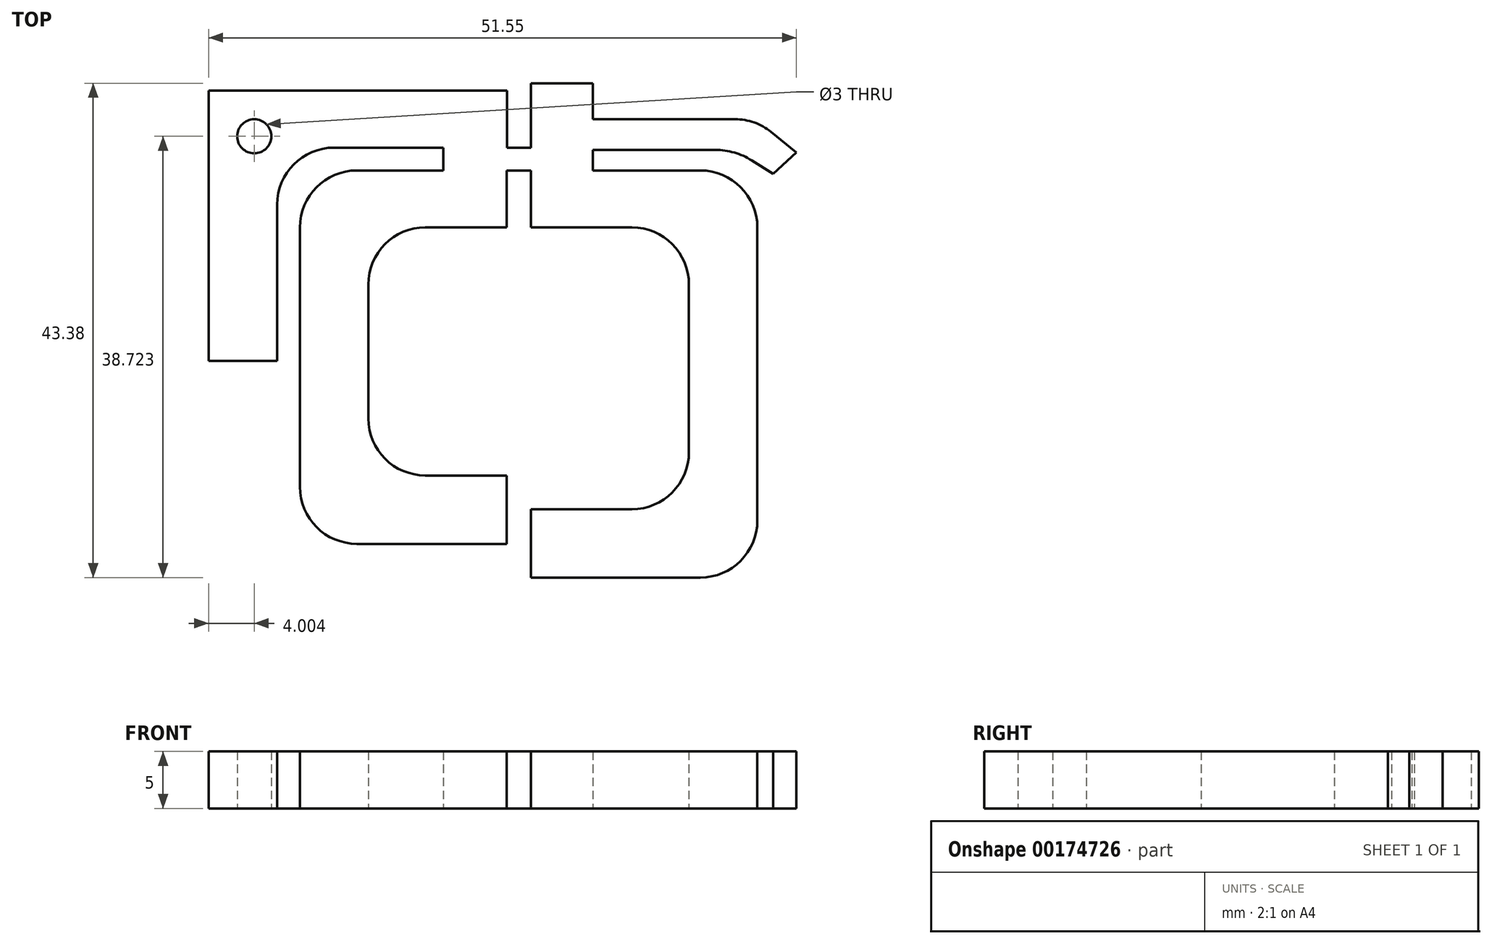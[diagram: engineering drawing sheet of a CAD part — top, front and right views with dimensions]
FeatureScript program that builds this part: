
annotation { "Feature Type Name" : "Feature", "Feature Type Description" : "" }
export const myFeature = defineFeature(function(context is Context, id is Id, definition is map)
    precondition{}
    {
        {
            var Q0;
            Q0=qCreatedBy(makeId("Top.planeOp"),FACE);
            var sketch = newSketch(context, id + "F0", { "sketchPlane" : qUnion([Q0])});
            skLineSegment(sketch, "E0.bottom", {"start": v(-10.9, 25.3) * mm, "end": v(-20.47, 25.3) * mm});
            skLineSegment(sketch, "E0.top", {"start": v(-5.3, 30.3) * mm, "end": v(-31.47, 30.3) * mm});
            skLineSegment(sketch, "E0.left", {"start": v(-5.3, 25.3) * mm, "end": v(-5.3, 30.3) * mm});
            skLineSegment(sketch, "E0.right", {"start": v(-31.47, 26.54) * mm, "end": v(-31.47, 30.3) * mm});
            skLineSegment(sketch, "E1.top", {"start": v(-31.47, 6.6) * mm, "end": v(-25.47, 6.6) * mm});
            skLineSegment(sketch, "E1.left", {"start": v(-31.47, 26.54) * mm, "end": v(-31.47, 6.6) * mm});
            skLineSegment(sketch, "E1.right", {"start": v(-25.47, 20.3) * mm, "end": v(-25.47, 6.6) * mm});
            skArc(sketch, "E2.filletArc", {"start": v(-20.47, 25.3) * mm, "mid": v(-24, 23.84) * mm, "end": v(-25.47, 20.3) * mm});
            skLineSegment(sketch, "E3.right", {"start": v(-10.9, 25.3) * mm, "end": v(-10.9, 23.3) * mm});
            skLineSegment(sketch, "E4.bottom", {"start": v(-10.9, 23.3) * mm, "end": v(-18.47, 23.3) * mm});
            skLineSegment(sketch, "E4.top", {"start": v(-5.33, 18.3) * mm, "end": v(-12.47, 18.3) * mm});
            skLineSegment(sketch, "E4.left", {"start": v(-5.33, 23.3) * mm, "end": v(-5.33, 18.3) * mm});
            skLineSegment(sketch, "E4.right", {"start": v(-23.47, 18.3) * mm, "end": v(-23.47, 9.2) * mm});
            skLineSegment(sketch, "E5.left", {"start": v(-23.47, 15.1) * mm, "end": v(-23.47, -4.46) * mm});
            skLineSegment(sketch, "E5.right", {"start": v(-17.47, 13.3) * mm, "end": v(-17.47, 1.54) * mm});
            skLineSegment(sketch, "E6.top", {"start": v(-12.47, -3.46) * mm, "end": v(-5.33, -3.46) * mm});
            skLineSegment(sketch, "E6.right", {"start": v(-5.33, -9.46) * mm, "end": v(-5.33, -3.46) * mm});
            skPoint(sketch, "E7.visualSharp", {"position": v(-23.47, 23.3) * mm});
            skArc(sketch, "E7.filletArc", {"start": v(-18.47, 23.3) * mm, "mid": v(-22, 21.84) * mm, "end": v(-23.47, 18.3) * mm});
            skArc(sketch, "E8.filletArc", {"start": v(-12.47, 18.3) * mm, "mid": v(-16, 16.84) * mm, "end": v(-17.47, 13.3) * mm});
            skPoint(sketch, "E9.visualSharp", {"position": v(-23.47, -9.46) * mm});
            skArc(sketch, "E9.filletArc", {"start": v(-23.47, -4.46) * mm, "mid": v(-22, -8) * mm, "end": v(-18.47, -9.46) * mm});
            skArc(sketch, "E10.filletArc", {"start": v(-17.47, 1.54) * mm, "mid": v(-16, -2) * mm, "end": v(-12.47, -3.46) * mm});
            skLineSegment(sketch, "E11.bottom", {"start": v(-5.3, 25.3) * mm, "end": v(-3.2, 25.3) * mm});
            skLineSegment(sketch, "E11.top", {"start": v(-5.33, 23.3) * mm, "end": v(-3.2, 23.3) * mm});
            skLineSegment(sketch, "E12.bottom", {"start": v(-3.2, 18.3) * mm, "end": v(2.2, 18.3) * mm});
            skLineSegment(sketch, "E12.top", {"start": v(-3.2, 30.96) * mm, "end": v(2.2, 30.96) * mm});
            skLineSegment(sketch, "E12.left", {"start": v(-3.2, 18.3) * mm, "end": v(-3.2, 23.3) * mm});
            skLineSegment(sketch, "E12.right", {"start": v(2.2, 23.3) * mm, "end": v(2.2, 25.1) * mm});
            skLineSegment(sketch, "E13.bottom", {"start": v(2.2, 23.3) * mm, "end": v(11.65, 23.3) * mm});
            skLineSegment(sketch, "E13.top", {"start": v(2.2, 18.3) * mm, "end": v(5.65, 18.3) * mm});
            skLineSegment(sketch, "E13.right", {"start": v(16.65, 18.3) * mm, "end": v(16.65, 18.3) * mm});
            skLineSegment(sketch, "E14.top", {"start": v(11.65, -12.42) * mm, "end": v(10.65, -12.42) * mm});
            skLineSegment(sketch, "E14.left", {"start": v(16.65, 18.3) * mm, "end": v(16.65, -7.42) * mm});
            skLineSegment(sketch, "E14.right", {"start": v(10.65, 13.3) * mm, "end": v(10.65, -1.42) * mm});
            skLineSegment(sketch, "E15.bottom", {"start": v(10.65, -12.42) * mm, "end": v(-3.2, -12.42) * mm});
            skLineSegment(sketch, "E15.top", {"start": v(5.65, -6.42) * mm, "end": v(-3.2, -6.42) * mm});
            skLineSegment(sketch, "E15.right", {"start": v(-3.2, -12.42) * mm, "end": v(-3.2, -6.42) * mm});
            skLineSegment(sketch, "E16.trimOffspring", {"start": v(-3.2, 25.3) * mm, "end": v(-3.2, 30.96) * mm});
            skPoint(sketch, "E17.visualSharp", {"position": v(16.65, 23.3) * mm});
            skArc(sketch, "E17.filletArc", {"start": v(16.65, 18.3) * mm, "mid": v(15.19, 21.84) * mm, "end": v(11.65, 23.3) * mm});
            skPoint(sketch, "E18.visualSharp", {"position": v(10.65, 18.3) * mm});
            skArc(sketch, "E18.filletArc", {"start": v(10.65, 13.3) * mm, "mid": v(9.19, 16.84) * mm, "end": v(5.65, 18.3) * mm});
            skPoint(sketch, "E19.visualSharp", {"position": v(16.65, -12.42) * mm});
            skArc(sketch, "E19.filletArc", {"start": v(11.65, -12.42) * mm, "mid": v(15.19, -10.95) * mm, "end": v(16.65, -7.42) * mm});
            skPoint(sketch, "E20.visualSharp", {"position": v(10.65, -6.42) * mm});
            skArc(sketch, "E20.filletArc", {"start": v(5.65, -6.42) * mm, "mid": v(9.19, -4.95) * mm, "end": v(10.65, -1.42) * mm});
            skLineSegment(sketch, "E21.trimOffspring", {"start": v(-18.47, -9.46) * mm, "end": v(-5.33, -9.46) * mm});
            skLineSegment(sketch, "E22", {"start": v(2.2, 27.8) * mm, "end": v(14.7, 27.8) * mm});
            skLineSegment(sketch, "E23", {"start": v(17.85, 26.68) * mm, "end": v(20.08, 24.87) * mm});
            skPoint(sketch, "E24.visualSharp", {"position": v(16.47, 27.8) * mm});
            skArc(sketch, "E24.filletArc", {"start": v(17.85, 26.68) * mm, "mid": v(16.37, 27.51) * mm, "end": v(14.7, 27.8) * mm});
            skLineSegment(sketch, "E25", {"start": v(2.2, 25.1) * mm, "end": v(12.96, 25.1) * mm});
            skLineSegment(sketch, "E26", {"start": v(18.02, 23) * mm, "end": v(16.16, 24.18) * mm});
            skPoint(sketch, "E27.visualSharp", {"position": v(14.7, 25.1) * mm});
            skArc(sketch, "E27.filletArc", {"start": v(16.16, 24.18) * mm, "mid": v(14.63, 24.87) * mm, "end": v(12.96, 25.1) * mm});
            skLineSegment(sketch, "E28", {"start": v(18.02, 23) * mm, "end": v(20.08, 24.87) * mm});
            skLineSegment(sketch, "E29.trimOffspring", {"start": v(2.2, 27.8) * mm, "end": v(2.2, 30.96) * mm});
            skCircle(sketch, "E30", {"center": v(-27.47, 26.3) * mm, "radius": 1.5 * mm});
            skSolve(sketch);
        }
        {
            var Q0;
            Q0 = qSketchRegion(id + "F0", true);
            var Q1;
            Q1=makeQuery(id+"F0.imprint","IMPRINT",FACE,{"disambiguationData":[TD([[makeQuery(id+"F0.imprint","IMPRINT",EDGE,{"derivedFrom":sQuery(id+"F0.wireOp",EDGE,"E0.bottom")}),-1.0]])]});
            extrude(context, id + "F1", {"entities" : qUnion([Q0, Q1]), "depth" : 5 * mm});
        }
    });
